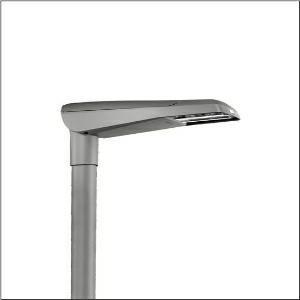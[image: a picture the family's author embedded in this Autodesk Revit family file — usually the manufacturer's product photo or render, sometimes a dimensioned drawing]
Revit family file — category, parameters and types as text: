
# Revit family: streetlight_sl_11_iq_micro___st1_2a_5xc1ac1f08de_2d80
name_source: partatom
category: Lighting Fixtures
units: mm (PartAtom-declared; Revit-internal decimal feet)

## family parameters
Cut with Voids When Loaded = No
Host = Face
Light Source = No
Part Type = Normal
Room Calculation Point = No
Round Connector Dimension = Use Diameter
Shared = No

## types (1)
- --- (1 x LED, 3860 lm, 27.4 W, 4000K)
    Apparent Load = 27 VA
    CIE Flux Codes = 33 71 96 100 100
    Color Rendering = 70
    Color Temperature = 4000K
    Default Elevation = 1800 mm
    Description = Streetlight SL 11 iQ micro, mast luminaire, primary light control with 3 zone facetted reflector, of plastic, silver coated, highly specular, primary optical cover: cover, of PMMA, transparent, light distribution: ST1.2a, light emission: direct distribution, primary light characteristic: asymmetric, installation type: post-top, side-entry, lamps: LED, High Power LED, rated values: 3.620lm | 27,7W | 130,7lm/W (begin service life); end service life: 3.620lm | 28,1W; at 50% lumin. flux: 1.810lm | 13,4W | 135,1lm/W, colour temperature: 2200/2700/3000/4000K, colour rendering: CRI > 70, light colour: 722/727/730/740, light setting 1 begin service life: 100% | 3.620lm | 27,7W | 130,7lm/W | 3.000K, light setting 1 end service life: 28,1W, further light settings possible, control: Street-Remote, Auto-Match, Temp-Guard, Lumen-Switch, Night-Set, Smart-Wire, Light-Fading, Desk-Remote (wireless, voltage-free reading and setting of iQ features in the workshop via application-optimized NFC function/RFID function), optimised constant luminous flux control (CLO 2.0), with cable H07RN-F 3x 1.5mm², mains connection: 220..240V, AC, 50/60Hz, connection cable pre-assembled, cable length: 6,5m, luminaire housing, of diecast aluminium, powder-coated, SITECO metallic grey (DB 702S), please order mast flange separately, inclination adjustable without tools: 0°, 5°, 10°, 15° (post-top) | 0°, -5°, -10°, -15° (side-entry), sealing non-destructively replaceable, multi-level sealing system, length: 600mm, width: 174mm, height: 116mm, mast flange for spigot size: 42mm (side-entry): 5XC10008XM4, 60/48mm (side-entry/post-top): 5XC10108XM2, 76/60mm (side-entry/post-top): 5XC10108XM1, equipment: Power, protection rating (complete): IP66, insulation class (complete): insulation class II (safety insulation), certification: CE, ENEC, ENEC+, VDE, impact resistance: IK10, permissible operating ambient temperature for outdoor applications: -25..+50°C, standard-compliant lighting for roads and squares, Environmental Product Declaration (EPD) tested and certified by an independent institute, packaging unit: 1 piece

Light Distribution: ST1.2a
    Height = 116 mm
    Lamp = 1 x LED
    Lamp Light Flux = 3860 lm
    Lamp Power = 27.4 W
    Lamp count = 1
    Length = 600 mm
    Luminous efficacy = 141 lm/W
    Manufacturer = Siteco
    ModVariant = No
    Model = 5XC1AC1F08DE
    Number of Poles = 1
    OnlyDefault = Yes
    Power Factor = 1
    Product Name = Streetlight SL 11 iQ micro | ST1.2a
    Product group = mast luminaire | pylon top
    ProductGroupID = 6100
    Protection Class = Protection class II
    Protection Degree = IP 66
    RLX_Detail_Level = 1
    RLX_Emergency_Light_Flux = 0 lm
    RLX_Emergency_Type = 0
    RLX_Emergency_Type_DB = No
    RlxData = <blob elided: 59533 chars, md5=2a10843a>
    Socket = socket
    Standby Power = 0 W
    System Light Flux = 3860 lm
    System Power = 27 W
    Type Comments = individual setting: luminous flux: 100 % | dim-lin: 254 | 726 mA
    Type Image = l_1006566.jpg
    URL = http://relux.com
    VarID = @adj_047477
    Voltage = 0 V
    Weight = 0.00 kg
    Width = 174 mm

## geometry (parser evidence)
native form markers: Blend x4, Sweep x12
no freeform markers — native parametric forms only
